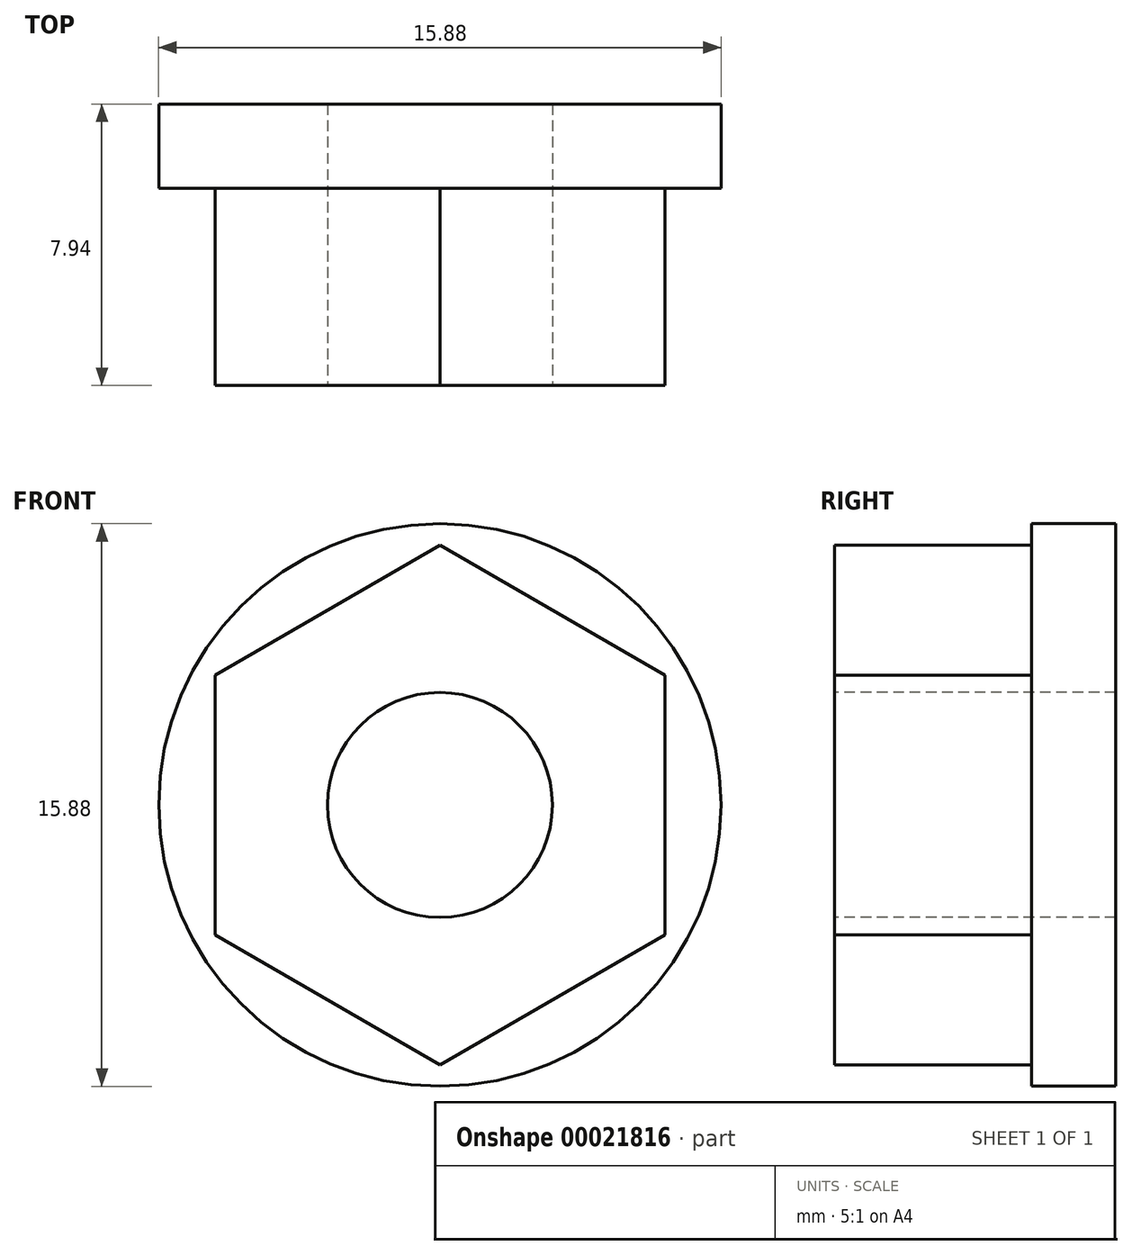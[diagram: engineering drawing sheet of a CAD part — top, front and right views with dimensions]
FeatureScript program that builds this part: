
annotation { "Feature Type Name" : "Feature", "Feature Type Description" : "" }
export const myFeature = defineFeature(function(context is Context, id is Id, definition is map)
    precondition{}
    {
        {
            var Q0;
            Q0=qCreatedBy(makeId("Front.planeOp"),FACE);
            var sketch = newSketch(context, id + "F0", { "sketchPlane" : qUnion([Q0])});
            skCircle(sketch, "E0", {"center": v(0, 0) * mm, "radius": 7.94 * mm});
            skSolve(sketch);
        }
        {
            var Q0;
            Q0=makeQuery(id+"F0.imprint","IMPRINT",FACE,{"disambiguationData":[TD([[makeQuery(id+"F0.imprint","IMPRINT",EDGE,{"derivedFrom":sQuery(id+"F0.wireOp",EDGE,"E0")}),1.0]])]});
            extrude(context, id + "F1", {"entities" : qUnion([Q0]), "depth" : 2.38 * mm});
        }
        {
            var Q0;
            Q0=makeQuery(id+"F1.opExtrude","CAP_FACE",FACE,{"disambiguationData":[OSD([sQuery(id+"F0.wireOp",EDGE,"E0")])],"isStart":false});
            var sketch = newSketch(context, id + "F2", { "sketchPlane" : qUnion([Q0])});
            skCircle(sketch, "E1.cCircle", {"center": v(0, 0) * mm, "radius": 6.35 * mm, "construction": true});
            skLineSegment(sketch, "E1.0", {"start": v(6.35, 3.67) * mm, "end": v(6.35, -3.67) * mm});
            skLineSegment(sketch, "E1.1", {"start": v(6.35, -3.67) * mm, "end": v(0, -7.33) * mm});
            skLineSegment(sketch, "E1.2", {"start": v(0, -7.33) * mm, "end": v(-6.35, -3.67) * mm});
            skLineSegment(sketch, "E1.3", {"start": v(-6.35, -3.67) * mm, "end": v(-6.35, 3.67) * mm});
            skLineSegment(sketch, "E1.4", {"start": v(-6.35, 3.67) * mm, "end": v(0, 7.33) * mm});
            skLineSegment(sketch, "E1.5", {"start": v(0, 7.33) * mm, "end": v(6.35, 3.67) * mm});
            skPoint(sketch, "E1.0.midPoint", {"position": v(6.35, 0) * mm});
            skSolve(sketch);
        }
        {
            var Q0;
            Q0=makeQuery(id+"F2.imprint","IMPRINT",FACE,{"disambiguationData":[TD([[makeQuery(id+"F2.imprint","IMPRINT",EDGE,{"derivedFrom":sQuery(id+"F2.wireOp",EDGE,"E1.0")}),-1.0]])]});
            extrude(context, id + "F3", {"entities" : qUnion([Q0]), "operationType" : NewBodyOperationType.ADD, "depth" : 5.56 * mm});
        }
        {
            var Q0;
            Q0=makeQuery(id+"F3.opExtrude","CAP_FACE",FACE,{"disambiguationData":[OSD([sQuery(id+"F2.wireOp",EDGE,"E1.0"),sQuery(id+"F2.wireOp",EDGE,"E1.1"),sQuery(id+"F2.wireOp",EDGE,"E1.2"),sQuery(id+"F2.wireOp",EDGE,"E1.3"),sQuery(id+"F2.wireOp",EDGE,"E1.4"),sQuery(id+"F2.wireOp",EDGE,"E1.5")])],"isStart":false});
            var sketch = newSketch(context, id + "F4", { "sketchPlane" : qUnion([Q0])});
            skCircle(sketch, "E2", {"center": v(0, 0) * mm, "radius": 3.18 * mm});
            skSolve(sketch);
        }
        {
            var Q0;
            Q0=makeQuery(id+"F4.imprint","IMPRINT",FACE,{"disambiguationData":[TD([[makeQuery(id+"F4.imprint","IMPRINT",EDGE,{"derivedFrom":sQuery(id+"F4.wireOp",EDGE,"E2")}),1.0]])]});
            extrude(context, id + "F5", {"entities" : qUnion([Q0]), "operationType" : NewBodyOperationType.REMOVE, "endBound" : BoundingType.THROUGH_ALL, "oppositeDirection" : true, "depth" : 25.4 * mm});
        }
    });
